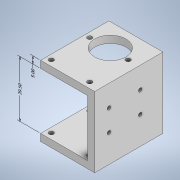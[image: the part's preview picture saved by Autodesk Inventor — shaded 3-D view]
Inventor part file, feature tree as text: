
AUTODESK INVENTOR PART (.ipt)
format: ipt  version: 2022 (Build 260153000, 153)  size: 171,008 bytes
history: native  units: mm
features: sketch x5, other x3, hole x3, extrude x2
ambient origin geometry x8: Origin, YZ Plane, XZ Plane, XY Plane, X Axis, Y Axis, Z Axis, Center Point
bodies: Body1 (feature_tree)
feature tree (13):
  other  "ソリッド1"
  extrude  "押し出し1"  Depth=48.0mm
  extrude  "押し出し2"  Depth=38.0mm
  hole  "穴1"  [1 undecoded]
  hole  "穴2"  [1 undecoded]
  hole  "穴4"  [1 undecoded]
  sketch  "スケッチ1"
  sketch  "スケッチ2"
  sketch  "スケッチ3"
  sketch  "スケッチ4"
  sketch  "スケッチ6"
  other  "長さ寸法 1"
  other  "長さ寸法 2"
note: 3 required parameter values undecoded (feature->parameter linkage not recoverable at this tier; creation-order binding heuristic only, values carry confidence <= 0.55)
